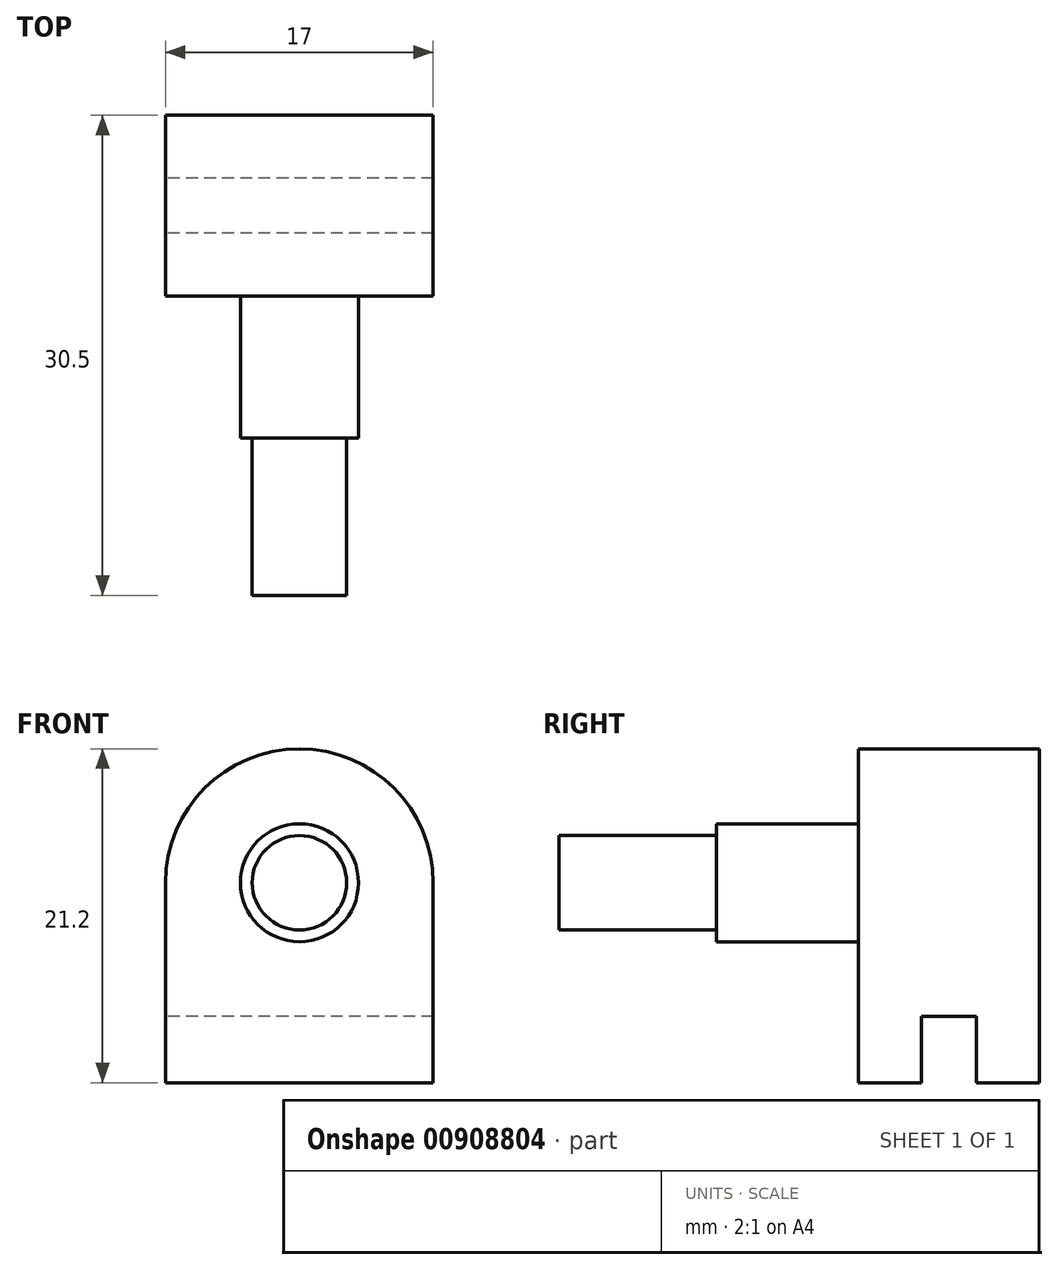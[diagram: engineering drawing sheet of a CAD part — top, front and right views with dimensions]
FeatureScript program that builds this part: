
annotation { "Feature Type Name" : "Feature", "Feature Type Description" : "" }
export const myFeature = defineFeature(function(context is Context, id is Id, definition is map)
    precondition{}
    {
        {
            var Q0;
            Q0=qCreatedBy(makeId("Front.planeOp"),FACE);
            var sketch = newSketch(context, id + "F0", { "sketchPlane" : qUnion([Q0])});
            skLineSegment(sketch, "E0.bottom", {"start": v(-8.5, -8.5) * mm, "end": v(8.5, -8.5) * mm});
            skLineSegment(sketch, "E0.top", {"start": v(-8.5, 8.5) * mm, "end": v(8.5, 8.5) * mm});
            skLineSegment(sketch, "E0.left", {"start": v(-8.5, -8.5) * mm, "end": v(-8.5, 8.5) * mm});
            skLineSegment(sketch, "E0.right", {"start": v(8.5, -8.5) * mm, "end": v(8.5, 8.5) * mm});
            skPoint(sketch, "E0.middle", {"position": v(0, 0) * mm});
            skSolve(sketch);
        }
        {
            var Q0;
            Q0=qSketchRegion(id+"F0",true);
            extrude(context, id + "F1", {"entities" : qUnion([Q0]), "offsetDistance" : 25 * mm, "depth" : 11.5 * mm});
        }
        {
            var Q0;
            Q0=makeQuery(id+"F1.opExtrude","CAP_FACE",FACE,{"disambiguationData":[OSD([sQuery(id+"F0.wireOp",EDGE,"E0.bottom"),sQuery(id+"F0.wireOp",EDGE,"E0.top"),sQuery(id+"F0.wireOp",EDGE,"E0.left"),sQuery(id+"F0.wireOp",EDGE,"E0.right")])],"isStart":false});
            var sketch = newSketch(context, id + "F2", { "sketchPlane" : qUnion([Q0])});
            skCircle(sketch, "E1", {"center": v(0, 0) * mm, "radius": 3.75 * mm});
            skSolve(sketch);
        }
        {
            var Q0;
            Q0=qSketchRegion(id+"F2",true);
            extrude(context, id + "F3", {"entities" : qUnion([Q0]), "operationType" : NewBodyOperationType.ADD, "depth" : 9 * mm});
        }
        {
            var Q0;
            Q0=makeQuery(id+"F3.opExtrude","CAP_FACE",FACE,{"disambiguationData":[OSD([sQuery(id+"F2.wireOp",EDGE,"E1")])],"isStart":false});
            var sketch = newSketch(context, id + "F4", { "sketchPlane" : qUnion([Q0])});
            skCircle(sketch, "E2", {"center": v(0, 0) * mm, "radius": 3 * mm});
            skSolve(sketch);
        }
        {
            var Q0;
            Q0=qSketchRegion(id+"F4",true);
            extrude(context, id + "F5", {"entities" : qUnion([Q0]), "operationType" : NewBodyOperationType.ADD, "depth" : 10 * mm});
        }
        {
            var Q0;
            Q0=makeQuery(id+"F1.opExtrude","SWEPT_FACE",FACE,{"disambiguationData":[OSD([sQuery(id+"F0.wireOp",EDGE,"E0.bottom")])]});
            var sketch = newSketch(context, id + "F6", { "sketchPlane" : qUnion([Q0])});
            skLineSegment(sketch, "E3.bottom", {"start": v(8.5, 0) * mm, "end": v(-8.5, 0) * mm});
            skLineSegment(sketch, "E3.top", {"start": v(8.5, 4) * mm, "end": v(-8.5, 4) * mm});
            skLineSegment(sketch, "E3.left", {"start": v(8.5, 0) * mm, "end": v(8.5, 4) * mm});
            skLineSegment(sketch, "E3.right", {"start": v(-8.5, 0) * mm, "end": v(-8.5, 4) * mm});
            skPoint(sketch, "E3.middle", {"position": v(0, 2) * mm});
            skLineSegment(sketch, "E4.bottom", {"start": v(8.5, 7.5) * mm, "end": v(-8.5, 7.5) * mm});
            skLineSegment(sketch, "E4.top", {"start": v(8.5, 11.5) * mm, "end": v(-8.5, 11.5) * mm});
            skLineSegment(sketch, "E4.left", {"start": v(8.5, 7.5) * mm, "end": v(8.5, 11.5) * mm});
            skLineSegment(sketch, "E4.right", {"start": v(-8.5, 7.5) * mm, "end": v(-8.5, 11.5) * mm});
            skPoint(sketch, "E4.middle", {"position": v(0, 9.5) * mm});
            skSolve(sketch);
        }
        {
            var Q0;
            Q0=qSketchRegion(id+"F6",true);
            extrude(context, id + "F7", {"entities" : qUnion([Q0]), "operationType" : NewBodyOperationType.ADD, "depth" : 4.2 * mm});
        }
        {
            var Q0;
            Q0=makeQuery(id+"F1.opExtrude","SWEPT_EDGE",EDGE,{"disambiguationData":[OSD([sQuery(id+"F0.wireOp",EDGE,"E0.top"),sQuery(id+"F0.wireOp",EDGE,"E0.right")])]});
            var Q1;
            Q1=makeQuery(id+"F1.opExtrude","SWEPT_EDGE",EDGE,{"disambiguationData":[OSD([sQuery(id+"F0.wireOp",EDGE,"E0.top"),sQuery(id+"F0.wireOp",EDGE,"E0.left")])]});
            fillet(context, id + "F8", {"entities" : qUnion([Q0, Q1]), "radius" : 8.5 * mm, "tangentPropagation" : true, "allowEdgeOverflow" : false});
        }
    });
